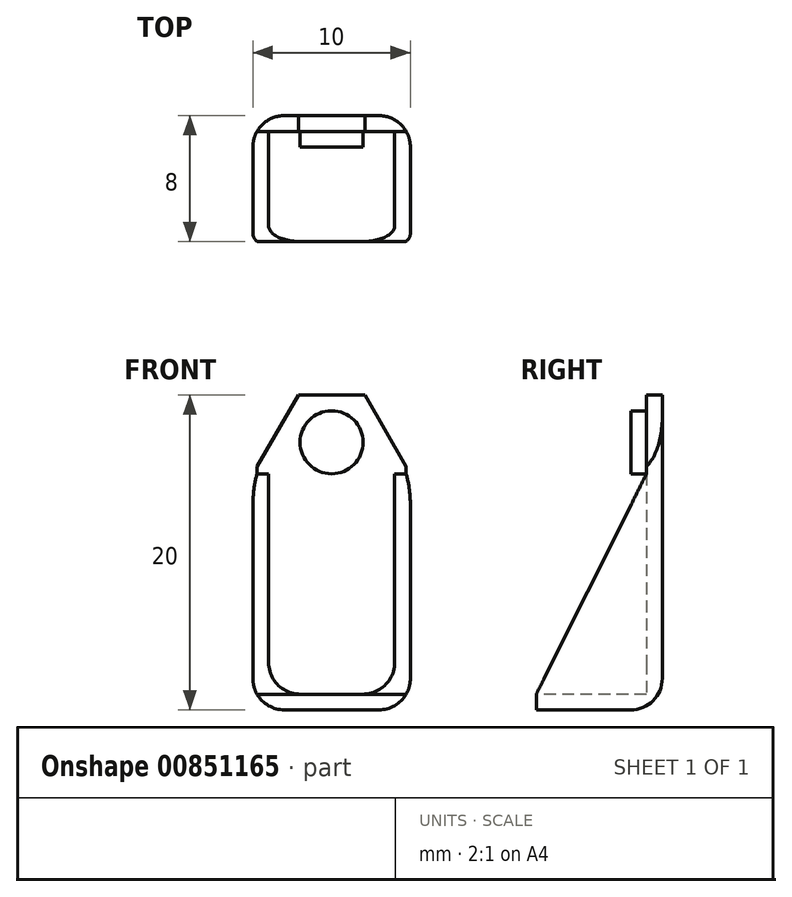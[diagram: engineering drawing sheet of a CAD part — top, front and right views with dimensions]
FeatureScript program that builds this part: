
annotation { "Feature Type Name" : "Feature", "Feature Type Description" : "" }
export const myFeature = defineFeature(function(context is Context, id is Id, definition is map)
    precondition{}
    {
        {
            var Q0;
            Q0=qCreatedBy(makeId("Front.planeOp"),FACE);
            var sketch = newSketch(context, id + "F0", { "sketchPlane" : qUnion([Q0])});
            skLineSegment(sketch, "E0.bottom", {"start": v(-5, 0) * mm, "end": v(5, 0) * mm});
            skLineSegment(sketch, "E0.top", {"start": v(-5, 15) * mm, "end": v(5, 15) * mm});
            skLineSegment(sketch, "E0.left", {"start": v(-5, 0) * mm, "end": v(-5, 15) * mm});
            skLineSegment(sketch, "E0.right", {"start": v(5, 0) * mm, "end": v(5, 15) * mm});
            skSolve(sketch);
        }
        {
            var Q0;
            Q0 = qSketchRegion(id + "F0", true);
            extrude(context, id + "F1", {"entities" : qUnion([Q0]), "depth" : 8 * mm, "offsetDistance" : 25 * mm});
        }
        {
            var Q0;
            Q0=makeQuery(id+"F1.opExtrude","CAP_FACE",FACE,{"disambiguationData":[OSD([sQuery(id+"F0.wireOp",EDGE,"E0.bottom"),sQuery(id+"F0.wireOp",EDGE,"E0.top"),sQuery(id+"F0.wireOp",EDGE,"E0.left"),sQuery(id+"F0.wireOp",EDGE,"E0.right")])],"isStart":false});
            var sketch = newSketch(context, id + "F2", { "sketchPlane" : qUnion([Q0])});
            skLineSegment(sketch, "E1.bottom", {"start": v(-4, 15) * mm, "end": v(4, 15) * mm});
            skLineSegment(sketch, "E1.top", {"start": v(-4, 1) * mm, "end": v(4, 1) * mm});
            skLineSegment(sketch, "E1.left", {"start": v(-4, 15) * mm, "end": v(-4, 1) * mm});
            skLineSegment(sketch, "E1.right", {"start": v(4, 15) * mm, "end": v(4, 1) * mm});
            skSolve(sketch);
        }
        {
            var Q0;
            Q0 = qSketchRegion(id + "F2", true);
            extrude(context, id + "F3", {"entities" : qUnion([Q0]), "operationType" : NewBodyOperationType.REMOVE, "oppositeDirection" : true, "depth" : 14 * mm, "offsetDistance" : 25 * mm});
        }
        {
            var Q0;
            Q0=makeQuery(id+"F1.opExtrude","SWEPT_FACE",FACE,{"disambiguationData":[OSD([sQuery(id+"F0.wireOp",EDGE,"E0.left")])]});
            var sketch = newSketch(context, id + "F4", { "sketchPlane" : qUnion([Q0])});
            skLineSegment(sketch, "E2", {"start": v(1, 15) * mm, "end": v(8, 1) * mm});
            skSolve(sketch);
        }
        {
            var Q0;
            Q0 = qSketchRegion(id + "F4", true);
            var Q1;
            {var subQ0=sQuery(id+"F4.wireOp",EDGE,"E2");Q1=makeQuery(id+"F4.imprint","IMPRINT",FACE,{"disambiguationData":[TD([[makeQuery(id+"F4.imprint","IMPRINT",EDGE,{"derivedFrom":subQ0}),1.0]])]});}
            extrude(context, id + "F5", {"entities" : qUnion([Q0, Q1]), "operationType" : NewBodyOperationType.REMOVE, "oppositeDirection" : true, "depth" : 25 * mm, "offsetDistance" : 25 * mm});
        }
        {
            var Q0;
            Q0=makeQuery(id+"F1.opExtrude","CAP_FACE",FACE,{"disambiguationData":[OSD([sQuery(id+"F0.wireOp",EDGE,"E0.bottom"),sQuery(id+"F0.wireOp",EDGE,"E0.top"),sQuery(id+"F0.wireOp",EDGE,"E0.left"),sQuery(id+"F0.wireOp",EDGE,"E0.right")])],"isStart":true});
            var sketch = newSketch(context, id + "F6", { "sketchPlane" : qUnion([Q0])});
            skLineSegment(sketch, "E3", {"start": v(5, 15) * mm, "end": v(2.11, 20) * mm});
            skLineSegment(sketch, "E4", {"start": v(2.11, 20) * mm, "end": v(-2.11, 20) * mm});
            skLineSegment(sketch, "E5", {"start": v(-2.11, 20) * mm, "end": v(-5, 15) * mm});
            skSolve(sketch);
        }
        {
            var Q0;
            Q0=makeQuery(id+"F6.imprint","IMPRINT",FACE,{"disambiguationData":[TD([[makeQuery(id+"F6.imprint","IMPRINT",EDGE,{"derivedFrom":sQuery(id+"F6.wireOp",EDGE,"E3")}),1.0]])]});
            extrude(context, id + "F7", {"entities" : qUnion([Q0]), "operationType" : NewBodyOperationType.ADD, "oppositeDirection" : true, "depth" : 1 * mm, "offsetDistance" : 25 * mm});
        }
        {
            var Q0;
            Q0=makeQuery(id+"F7.opExtrude","CAP_FACE",FACE,{"disambiguationData":[OSD([sQuery(id+"F0.wireOp",EDGE,"E0.bottom"),sQuery(id+"F0.wireOp",EDGE,"E0.top"),sQuery(id+"F0.wireOp",EDGE,"E0.left"),sQuery(id+"F0.wireOp",EDGE,"E0.right"),sQuery(id+"F2.wireOp",EDGE,"E1.top"),sQuery(id+"F2.wireOp",EDGE,"E1.left"),sQuery(id+"F2.wireOp",EDGE,"E1.right"),sQuery(id+"F6.wireOp",EDGE,"E3"),sQuery(id+"F6.wireOp",EDGE,"E4"),sQuery(id+"F6.wireOp",EDGE,"E5")])],"isStart":false});
            var sketch = newSketch(context, id + "F8", { "sketchPlane" : qUnion([Q0])});
            skCircle(sketch, "E6", {"center": v(0, 17) * mm, "radius": 2 * mm});
            skSolve(sketch);
        }
        {
            var Q0;
            Q0 = qSketchRegion(id + "F8", true);
            extrude(context, id + "F9", {"entities" : qUnion([Q0]), "operationType" : NewBodyOperationType.ADD, "depth" : 1 * mm, "offsetDistance" : 25 * mm});
        }
        {
            var Q0;
            Q0=makeQuery(id+"F1.opExtrude","CAP_EDGE",EDGE,{"disambiguationData":[OSD([sQuery(id+"F0.wireOp",EDGE,"E0.bottom")])],"isStart":true});
            var Q1;
            Q1=makeQuery(id+"F3.boolean.opBoolean","COPY",EDGE,{"derivedFrom":makeQuery(id+"F3.opExtrude","CAP_EDGE",EDGE,{"disambiguationData":[OSD([sQuery(id+"F2.wireOp",EDGE,"E1.top")])],"isStart":false})});
            var Q2;
            Q2=makeQuery(id+"F1.opExtrude","CAP_EDGE",EDGE,{"disambiguationData":[OSD([sQuery(id+"F0.wireOp",EDGE,"E0.left")])],"isStart":true});
            var Q3;
            Q3=makeQuery(id+"F1.opExtrude","SWEPT_EDGE",EDGE,{"disambiguationData":[OSD([sQuery(id+"F0.wireOp",EDGE,"E0.bottom"),sQuery(id+"F0.wireOp",EDGE,"E0.left")])]});
            var Q4;
            Q4=makeQuery(id+"F1.opExtrude","SWEPT_EDGE",EDGE,{"disambiguationData":[OSD([sQuery(id+"F0.wireOp",EDGE,"E0.bottom"),sQuery(id+"F0.wireOp",EDGE,"E0.right")])]});
            var Q5;
            Q5=makeQuery(id+"F1.opExtrude","CAP_EDGE",EDGE,{"disambiguationData":[OSD([sQuery(id+"F0.wireOp",EDGE,"E0.right")])],"isStart":true});
            var Q6;
            Q6=makeQuery(id+"F3.boolean.opBoolean","COPY",EDGE,{"derivedFrom":makeQuery(id+"F3.opExtrude","SWEPT_EDGE",EDGE,{"disambiguationData":[OSD([sQuery(id+"F2.wireOp",EDGE,"E1.top"),sQuery(id+"F2.wireOp",EDGE,"E1.left")])]})});
            var Q7;
            Q7=makeQuery(id+"F3.boolean.opBoolean","COPY",EDGE,{"derivedFrom":makeQuery(id+"F3.opExtrude","SWEPT_EDGE",EDGE,{"disambiguationData":[OSD([sQuery(id+"F2.wireOp",EDGE,"E1.top"),sQuery(id+"F2.wireOp",EDGE,"E1.right")])]})});
            var Q8;
            Q8=makeQuery(id+"F7.opExtrude","CAP_EDGE",EDGE,{"disambiguationData":[OSD([sQuery(id+"F0.wireOp",EDGE,"E0.bottom"),sQuery(id+"F0.wireOp",EDGE,"E0.top"),sQuery(id+"F0.wireOp",EDGE,"E0.left"),sQuery(id+"F0.wireOp",EDGE,"E0.right"),sQuery(id+"F2.wireOp",EDGE,"E1.right")])],"isStart":false});
            var Q9;
            Q9=makeQuery(id+"F7.opExtrude","CAP_EDGE",EDGE,{"disambiguationData":[OSD([sQuery(id+"F0.wireOp",EDGE,"E0.bottom"),sQuery(id+"F0.wireOp",EDGE,"E0.top"),sQuery(id+"F0.wireOp",EDGE,"E0.left"),sQuery(id+"F0.wireOp",EDGE,"E0.right"),sQuery(id+"F2.wireOp",EDGE,"E1.left")])],"isStart":false});
            var Q10;
            Q10=makeQuery(id+"F7.opExtrude","CAP_EDGE",EDGE,{"disambiguationData":[OSD([sQuery(id+"F0.wireOp",EDGE,"E0.bottom"),sQuery(id+"F0.wireOp",EDGE,"E0.top"),sQuery(id+"F0.wireOp",EDGE,"E0.left"),sQuery(id+"F0.wireOp",EDGE,"E0.right"),sQuery(id+"F2.wireOp",EDGE,"E1.top")])],"isStart":false});
            fillet(context, id + "F10", {"entities" : qUnion([Q0, Q1, Q2, Q3, Q4, Q5, Q6, Q7, Q8, Q9, Q10]), "radius" : 2 * mm, "tangentPropagation" : true, "allowEdgeOverflow" : false});
        }
    });
